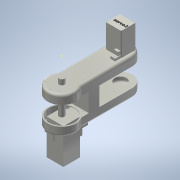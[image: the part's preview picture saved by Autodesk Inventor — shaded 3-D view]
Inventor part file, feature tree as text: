
AUTODESK INVENTOR PART (.ipt)
format: ipt  version: 2021 (Build 250183000, 183)  size: 585,728 bytes
history: native  units: mm (DEFAULTED — no unit token found)
features: sketch x42, extrude x23, hole x12, other x1, shell x1, revolve x1
ambient origin geometry x8: Origin, YZ Plane, XZ Plane, XY Plane, X Axis, Y Axis, Z Axis, Center Point
bodies: Solid1 (feature_tree)
feature tree (80):
  other  "作業平面1"
  extrude  "押し出し1"  Depth=120.0mm
  extrude  "押し出し2"  Depth=100.0mm
  shell  "Shell1"  Thickness=38.0mm
  hole  "Hole1"  [1 undecoded]
  hole  "Hole2"  [1 undecoded]
  hole  "Hole3"  [1 undecoded]
  hole  "Hole4"  [1 undecoded]
  extrude  "Extrusion3"  Depth=30.0mm TaperAngle=0.0deg
  sketch  "Sketch9"  dims[d12=50.0mm d13=6.0mm d14=4.0mm d15=2.0mm d16=14.3117mm d17=2.0mm d18=20.594885mm]
  extrude  "Extrusion4"  Depth=150.0mm TaperAngle=0.0deg
  sketch  "Sketch11"  dims[d26=50.0mm d27=6.0mm d28=4.0mm d29=2.0mm d30=14.3117mm d31=2.0mm d32=20.594885mm]
  extrude  "Extrusion6"  Depth=11.0mm TaperAngle=0.0deg
  extrude  "Extrusion7"  Depth=2.0mm TaperAngle=0.0deg
  sketch  "Sketch16"  dims[d52=30.0mm d53=0.0mm d54=30.0mm d55=0.0mm]
  revolve  "Revolution2"  [1 undecoded]
  extrude  "Extrusion8"  Depth=100.0mm TaperAngle=0.0deg
  extrude  "Extrusion9"  Depth=10.0mm TaperAngle=0.0deg
  extrude  "Extrusion10"  Depth=2.0mm TaperAngle=0.0deg
  hole  "Hole5"  [1 undecoded]
  hole  "Hole6"  [1 undecoded]
  sketch  "Sketch23"  dims[d88=2.438mm d89=6.0mm d90=4.369mm d91=2.0mm d92=14.3117mm d93=8.0mm d94=20.594885mm d95=8.0mm d96=0.0mm]
  extrude  "Extrusion11"  Depth=120.0mm
  extrude  "Extrusion12"  Depth=0.5mm
  hole  "Hole7"  [1 undecoded]
  hole  "Hole8"  [1 undecoded]
  extrude  "Extrusion13"  [1 undecoded]
  extrude  "Extrusion14"  [1 undecoded]
  hole  "Hole9"  [1 undecoded]
  hole  "Hole10"  [1 undecoded]
  extrude  "Extrusion15"  [1 undecoded]
  extrude  "Extrusion16"  [1 undecoded]
  sketch  "Sketch33"  dims[d145=120.0mm d146=0.0mm d46=0.5mm]
  extrude  "Extrusion17"  [1 undecoded]
  extrude  "Extrusion18"  [1 undecoded]
  hole  "Hole11"  [1 undecoded]
  hole  "Hole12"  [1 undecoded]
  sketch  "Sketch38"
  sketch  "Sketch39"
  sketch  "Sketch40"
  extrude  "Extrusion19"  [1 undecoded]
  extrude  "Extrusion20"  [1 undecoded]
  extrude  "Extrusion21"  [1 undecoded]
  extrude  "Extrusion22"  [1 undecoded]
  extrude  "Extrusion23"  [1 undecoded]
  extrude  "Extrusion24"  [1 undecoded]
  sketch  "Sketch47"
  sketch  "Sketch4"  dims[d0=40.0mm d1=120.0mm]
  sketch  "Sketch5"  dims[d2=250.0mm d3=100.0mm d4=38.0mm d5=0.0mm]
  sketch  "Sketch6"  dims[d6=10.0mm d7=65.0mm]
  sketch  "Sketch7"  dims[d8=140.0mm d9=10.0mm d10=0.0mm]
  sketch  "Sketch8"  dims[d11=2.0mm]
  sketch  "Sketch10"  dims[d19=50.0mm d20=6.0mm d21=4.0mm d22=2.0mm d23=14.3117mm d24=2.0mm d25=20.594885mm]
  sketch  "Sketch14"  dims[d33=50.0mm d34=6.0mm d35=4.0mm d36=2.0mm d37=14.3117mm d38=2.0mm d39=20.594885mm d40=150.0mm d41=0.0mm]
  sketch  "Sketch15"  dims[d42=60.0mm d43=0.0mm d44=30.0mm d45=0.0mm]
  sketch  "Sketch17"  dims[d56=180.0deg d57=150.0mm d58=0.0mm]
  sketch  "Sketch18"  dims[d59=11.0mm d60=0.0mm d61=11.0mm d62=0.0mm]
  sketch  "Sketch19"  dims[d63=2.438mm d64=6.0mm d65=4.369mm d66=2.0mm d67=14.3117mm d68=8.0mm d69=20.594885mm]
  sketch  "Sketch20"  dims[d70=2.438mm d71=6.0mm d72=4.369mm d73=2.0mm d74=14.3117mm d75=8.0mm d76=20.594885mm d77=8.0mm d78=0.0mm]
  sketch  "Sketch21"  dims[d79=8.0mm d80=0.0mm]
  sketch  "Sketch22"  dims[d81=2.438mm d82=6.0mm d83=4.369mm d84=2.0mm d85=14.3117mm d86=8.0mm d87=20.594885mm]
  sketch  "Sketch24"  dims[d97=8.0mm d98=0.0mm]
  sketch  "Sketch25"  dims[d99=2.438mm d100=6.0mm d101=4.369mm d102=2.0mm d103=14.3117mm d104=8.0mm d105=20.594885mm]
  sketch  "Sketch26"  dims[d106=2.438mm d107=6.0mm d108=4.369mm d109=2.0mm d110=14.3117mm d111=8.0mm d112=20.594885mm d113=100.0mm d114=0.0mm]
  sketch  "Sketch27"  dims[d115=9.0mm d116=0.0mm d117=10.0mm d118=0.0mm]
  sketch  "Sketch28"  dims[d119=10.0mm d120=0.0mm]
  sketch  "Sketch29"  dims[d121=2.438mm d122=6.0mm d123=4.369mm d124=2.0mm d125=14.3117mm d126=8.0mm d127=20.594885mm]
  sketch  "Sketch30"  dims[d128=2.438mm d129=6.0mm d130=4.369mm d131=2.0mm d132=14.3117mm d133=8.0mm d134=20.594885mm d135=2.0mm d136=0.0mm]
  sketch  "Sketch31"  dims[d137=1.0mm d138=0.0mm d139=130.0mm d140=0.0mm]
  sketch  "Sketch32"  dims[d141=80.0mm d142=0.0mm d143=80.0mm d144=0.0mm]
  sketch  "Sketch34"  dims[d47=0.872665mm d48=0.5mm]
  sketch  "Sketch35"  dims[d49=0.872665mm d50=0.5mm]
  sketch  "Sketch36"  dims[d51=0.872665mm]
  sketch  "Sketch37"
  sketch  "Sketch41"
  sketch  "Sketch42"
  sketch  "Sketch43"
  sketch  "Sketch44"
  sketch  "Sketch45"
  sketch  "Sketch46"
note: 25 required parameter values undecoded (feature->parameter linkage not recoverable at this tier; creation-order binding heuristic only, values carry confidence <= 0.55)